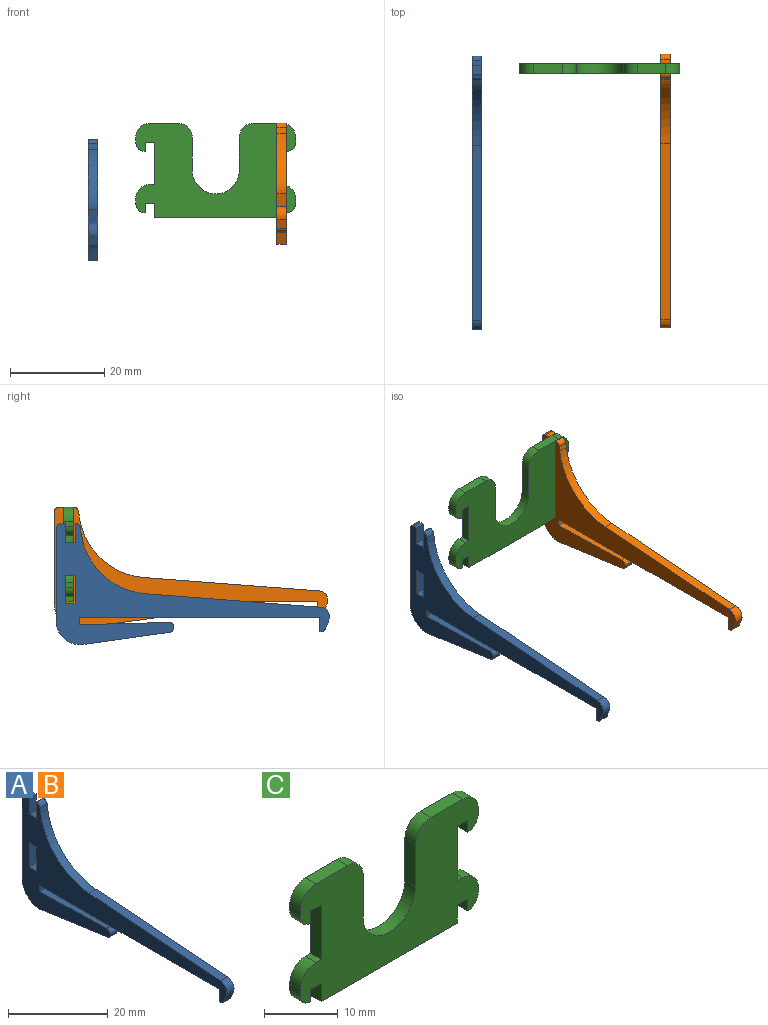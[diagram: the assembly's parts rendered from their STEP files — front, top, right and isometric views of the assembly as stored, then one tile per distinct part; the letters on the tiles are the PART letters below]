
ASSEMBLY  parts=3 mates=1
PART A: 30 faces, bbox 2x58.1x25.8 mm
  f0: plane 4x2mm, normal (0,-1,0), area 8mm2, adj f1,f19,f20,f21
  f1: plane 2x2mm, normal (0,0,1), area 4mm2, adj f0,f2,f20,f21
  f2: plane 4x2mm, normal (0,1,0), area 8mm2, adj f1,f3,f20,f21
  f3: plane 2x0.13mm, normal (0,0,1), area 0.3mm2, adj f2,f20,f21,f22
  f4: plane 2x1.23mm, normal (0,-0.99,0.14), area 2.5mm2, adj f20,f21,f22,f28
  f5: plane 37.29x2.87mm, normal (0,-0.08,1), area 74.8mm2, adj f20,f21,f28,f29
  f6: plane 2x1.84mm, normal (0,-0.93,-0.37), area 4mm2, adj f20,f21,f23,f29
  f7: plane 2x0.32mm, normal (0,0,-1), area 0.6mm2, adj f8,f20,f21,f23
  f8: plane 3x2mm, normal (0,1,0), area 6mm2, adj f7,f9,f20,f21
  f9: plane 51x2mm, normal (0,0,-1), area 102mm2, adj f8,f10,f20,f21
  f10: plane 2x1.5mm, normal (0,-1,0), area 3mm2, adj f9,f11,f20,f21
  f11: plane 18.98x2mm, normal (0,0.02,1), area 38mm2, adj f10,f20,f21,f24
  f12: plane 2x0.11mm, normal (0,-1,0), area 0.2mm2, adj f20,f21,f24,f25
  f13: plane 18.45x2.58mm, normal (0,-0.14,-0.99), area 37.3mm2, adj f20,f21,f25,f27
  f14: plane 19.75x2mm, normal (0,1,0), area 39.5mm2, adj f20,f21,f26,f27
  f15: plane 6x2mm, normal (0,1,0), area 12mm2, adj f16,f18,f20,f21
  f16: plane 2x2mm, normal (0,0,-1), area 4mm2, adj f15,f17,f20,f21
  f17: plane 6x2mm, normal (0,-1,0), area 12mm2, adj f16,f18,f20,f21
  f18: plane 2x2mm, normal (0,0,1), area 4mm2, adj f15,f17,f20,f21
  f19: plane 2x1mm, normal (0,0,1), area 2mm2, adj f0,f20,f21,f26
  f20: plane 58.13x25.75mm, normal (1,0,0), area 430.2mm2, adj f0,f1,f2,f3,f4,f5,f6,f7
  f21: plane 58.13x25.75mm, normal (-1,0,0), area 430.2mm2, adj f0,f1,f2,f3,f4,f5,f6,f7
  f22: cylinder r=1mm len=2mm, axis (1,0,0), area 2.9mm2, adj f3,f4,f20,f21
  f23: cylinder r=1mm len=2mm, axis (-1,0,0), area 2.4mm2, adj f6,f7,f20,f21
  f24: cylinder r=1mm len=2mm, axis (-1,0,0), area 3.2mm2, adj f11,f12,f20,f21
  f25: cylinder r=1mm len=2mm, axis (-1,0,0), area 2.9mm2, adj f12,f13,f20,f21
  f26: cylinder r=1mm len=2mm, axis (1,0,0), area 3.1mm2, adj f14,f19,f20,f21
  f27: cylinder r=5mm len=5.69mm, axis (1,0,0), area 17.1mm2, adj f13,f14,f20,f21
  f28: cylinder r=15mm len=13.7mm, axis (1,0,0), area 40.6mm2, adj f4,f5,f20,f21
  f29: cylinder r=2mm len=2.74mm, axis (1,0,0), area 7.5mm2, adj f5,f6,f20,f21
PART B: same geometry as A
PART C: 36 faces, bbox 34x2x20 mm
  f0: plane 2x1mm, normal (1,0,0), area 2mm2, adj f23,f24,f28,f30
  f1: plane 2x1mm, normal (0,0,1), area 2mm2, adj f2,f23,f24,f30
  f2: plane 9x2mm, normal (1,0,0), area 18mm2, adj f1,f3,f23,f24
  f3: plane 2x2mm, normal (0,0,-1), area 4mm2, adj f2,f4,f23,f24
  f4: plane 2x2mm, normal (-1,0,0), area 4mm2, adj f3,f23,f24,f25
  f5: plane 2x1mm, normal (1,0,0), area 2mm2, adj f23,f24,f25,f31
  f6: plane 6x2mm, normal (0,0,1), area 12mm2, adj f23,f24,f31,f32
  f7: plane 7x2mm, normal (-1,0,0), area 14mm2, adj f23,f24,f29,f32
  f8: plane 7x2mm, normal (1,0,0), area 14mm2, adj f23,f24,f29,f33
  f9: plane 6x2mm, normal (0,0,1), area 12mm2, adj f23,f24,f33,f34
  f10: plane 2x1mm, normal (-1,0,0), area 2mm2, adj f23,f24,f26,f34
  f11: plane 2x2mm, normal (1,0,0), area 4mm2, adj f12,f23,f24,f26
  f12: plane 2x2mm, normal (0,0,-1), area 4mm2, adj f11,f13,f23,f24
  f13: plane 9x2mm, normal (-1,0,0), area 18mm2, adj f12,f14,f23,f24
  f14: plane 2x1mm, normal (0,0,1), area 2mm2, adj f13,f23,f24,f35
  f15: plane 2x1mm, normal (-1,0,0), area 2mm2, adj f23,f24,f27,f35
  f16: plane 2x2mm, normal (1,0,0), area 4mm2, adj f17,f23,f24,f27
  f17: plane 2x2mm, normal (0,0,-1), area 4mm2, adj f16,f18,f23,f24
  f18: plane 3x2mm, normal (-1,0,0), area 6mm2, adj f17,f19,f23,f24
  f19: plane 26x2mm, normal (0,0,-1), area 52mm2, adj f18,f20,f23,f24
  f20: plane 3x2mm, normal (1,0,0), area 6mm2, adj f19,f21,f23,f24
  f21: plane 2x2mm, normal (0,0,-1), area 4mm2, adj f20,f22,f23,f24
  f22: plane 2x2mm, normal (-1,0,0), area 4mm2, adj f21,f23,f24,f28
  f23: plane 34x20mm, normal (0,-1,0), area 445.7mm2, adj f0,f1,f2,f3,f4,f5,f6,f7
  f24: plane 34x20mm, normal (0,1,0), area 445.7mm2, adj f0,f1,f2,f3,f4,f5,f6,f7
  f25: cylinder r=2mm len=2mm, axis (0,1,0), area 6.3mm2, adj f4,f5,f23,f24
  f26: cylinder r=2mm len=2mm, axis (0,1,0), area 6.3mm2, adj f10,f11,f23,f24
  f27: cylinder r=2mm len=2mm, axis (0,1,0), area 6.3mm2, adj f15,f16,f23,f24
  f28: cylinder r=2mm len=2mm, axis (0,1,0), area 6.3mm2, adj f0,f22,f23,f24
  f29: cylinder r=5mm len=10mm, axis (0,-1,0), area 31.4mm2, adj f7,f8,f23,f24
  f30: cylinder r=3mm len=3mm, axis (0,1,0), area 9.4mm2, adj f0,f1,f23,f24
  f31: cylinder r=3mm len=3mm, axis (0,-1,0), area 9.4mm2, adj f5,f6,f23,f24
  f32: cylinder r=3mm len=3mm, axis (0,1,0), area 9.4mm2, adj f6,f7,f23,f24
  f33: cylinder r=3mm len=3mm, axis (0,1,0), area 9.4mm2, adj f8,f9,f23,f24
  f34: cylinder r=3mm len=3mm, axis (0,-1,0), area 9.4mm2, adj f9,f10,f23,f24
  f35: cylinder r=3mm len=3mm, axis (0,1,0), area 9.4mm2, adj f14,f15,f23,f24
PLACE A t=(-33.03,-0.18,-1.93)mm
PLACE B t=(7.07,0.2,1.52)mm
PLACE C t=(7.07,23.2,1.52)mm
MATE fastened C.f24 <-> B.f17  axis (0,1,0) through (7.07,23.2,5.52)mm
